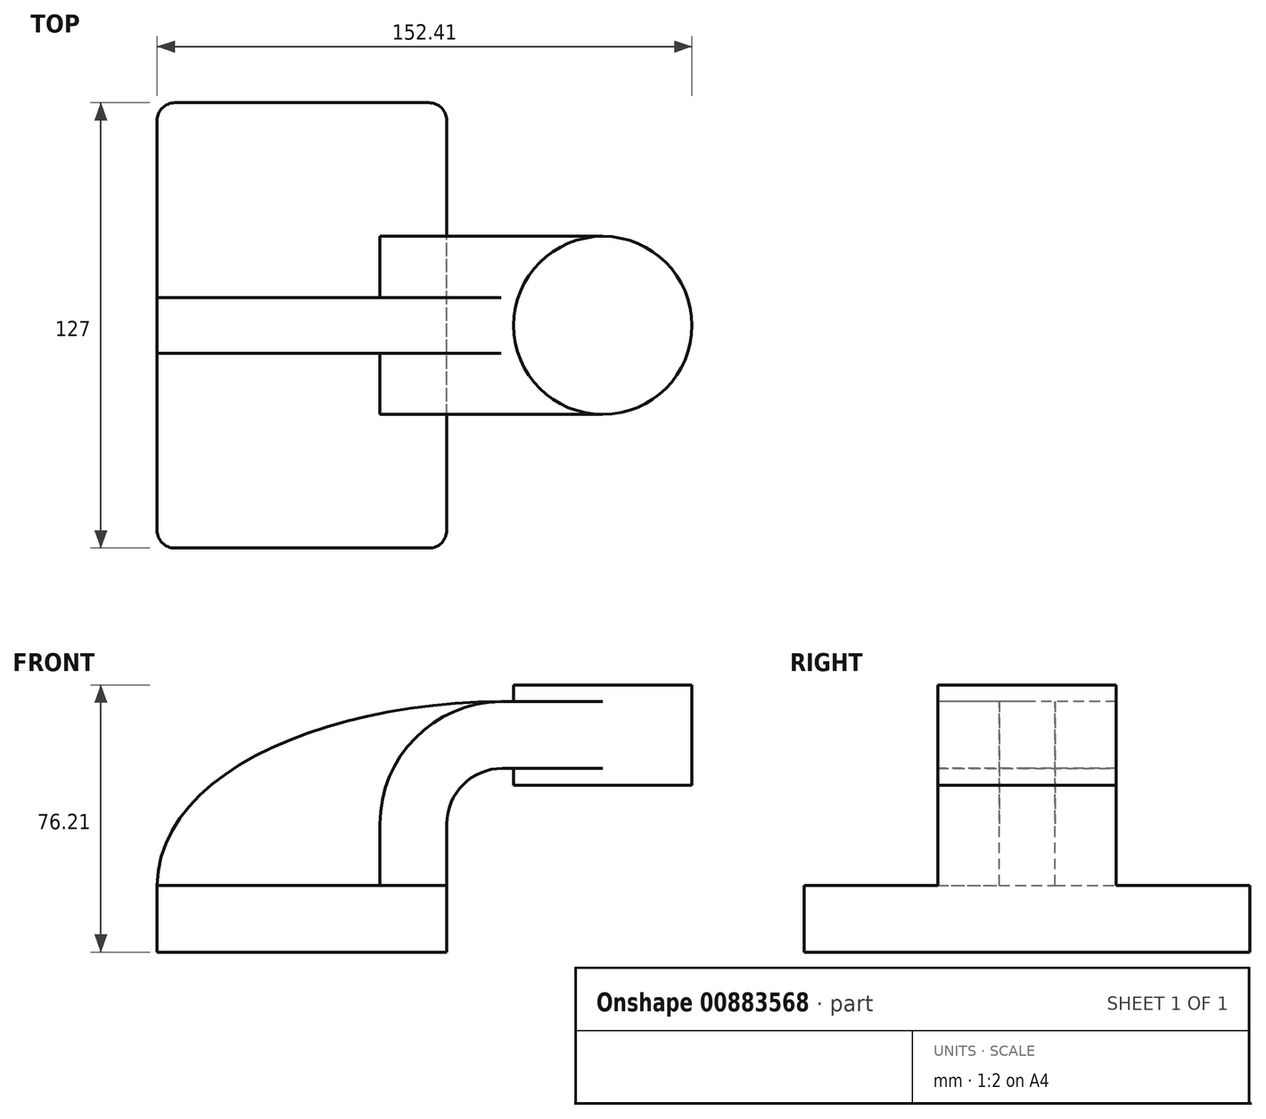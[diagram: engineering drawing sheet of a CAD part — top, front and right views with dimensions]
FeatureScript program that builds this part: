
annotation { "Feature Type Name" : "Feature", "Feature Type Description" : "" }
export const myFeature = defineFeature(function(context is Context, id is Id, definition is map)
    precondition{}
    {
        {
            var Q0;
            Q0=qCreatedBy(makeId("Front.planeOp"),FACE);
            var sketch = newSketch(context, id + "F0", { "sketchPlane" : qUnion([Q0])});
            skLineSegment(sketch, "E0.bottom", {"start": v(-41.28, -9.53) * mm, "end": v(41.28, -9.53) * mm});
            skLineSegment(sketch, "E0.top", {"start": v(-41.28, 9.52) * mm, "end": v(41.28, 9.52) * mm});
            skLineSegment(sketch, "E0.left", {"start": v(-41.28, -9.53) * mm, "end": v(-41.28, 9.53) * mm});
            skLineSegment(sketch, "E0.right", {"start": v(41.28, -9.53) * mm, "end": v(41.28, 9.52) * mm});
            skPoint(sketch, "E0.middle", {"position": v(0, 0) * mm});
            skLineSegment(sketch, "E1.bottom", {"start": v(111.12, 38.1) * mm, "end": v(60.32, 38.1) * mm});
            skLineSegment(sketch, "E1.top", {"start": v(111.12, 66.67) * mm, "end": v(60.32, 66.67) * mm});
            skLineSegment(sketch, "E1.left", {"start": v(111.12, 38.1) * mm, "end": v(111.12, 66.68) * mm});
            skLineSegment(sketch, "E1.right", {"start": v(60.32, 38.1) * mm, "end": v(60.32, 66.68) * mm});
            skPoint(sketch, "E1.middle", {"position": v(85.72, 52.39) * mm});
            skLineSegment(sketch, "E2", {"start": v(41.28, 9.52) * mm, "end": v(41.28, 27) * mm});
            skArc(sketch, "E3", {"start": v(41.27, 27) * mm, "mid": v(45.92, 38.23) * mm, "end": v(57.15, 42.88) * mm});
            skLineSegment(sketch, "E4", {"start": v(57.15, 42.88) * mm, "end": v(85.72, 42.88) * mm});
            skLineSegment(sketch, "E5.0", {"start": v(57.15, 61.93) * mm, "end": v(85.72, 61.93) * mm});
            skArc(sketch, "E5.1", {"start": v(22.22, 27) * mm, "mid": v(32.45, 51.7) * mm, "end": v(57.15, 61.93) * mm});
            skLineSegment(sketch, "E5.2", {"start": v(22.22, 9.52) * mm, "end": v(22.22, 27) * mm});
            skLineSegment(sketch, "E6", {"start": v(85.72, 38.1) * mm, "end": v(85.72, 66.67) * mm});
            skFitSpline(sketch, "E7", {"points": [v(-41.28, 9.52) * mm, v(57.15, 61.93) * mm], "startDerivative": vector(1.2, 96.26) * mm, "endDerivative": vector(151.74, 0.75) * mm});
            skSolve(sketch);
        }
        {
            var Q0;
            Q0=makeQuery(id+"F0.imprint","IMPRINT",FACE,{"disambiguationData":[TD([[makeQuery(id+"F0.imprint","IMPRINT",EDGE,{"derivedFrom":sQuery(id+"F0.wireOp",EDGE,"E0.bottom")}),1.0]])]});
            extrude(context, id + "F1", {"entities" : qUnion([Q0]), "endBound" : BoundingType.SYMMETRIC, "depth" : 127 * mm, "offsetDistance" : 25.4 * mm});
        }
        {
            var Q0;
            {var subQ1=sQuery(id+"F0.wireOp",EDGE,"E2");Q0=makeQuery(id+"F0.imprint","IMPRINT",FACE,{"disambiguationData":[TD([[makeQuery(id+"F0.imprint","IMPRINT",EDGE,{"derivedFrom":subQ1}),1.0]])]});}
            var Q1;
            {var subQ0=sQuery(id+"F0.wireOp",EDGE,"E4");var subQ1=sQuery(id+"F0.wireOp",EDGE,"E1.right");var subQ2=makeQuery(id+"F0.imprint","INTERSECT",VERTEX,{"derivedFrom":[subQ1,subQ0]});Q1=makeQuery(id+"F0.imprint","IMPRINT",FACE,{"disambiguationData":[TD([[makeQuery(id+"F0.imprint","IMPRINT",EDGE,{"disambiguationData":[TD([[subQ2,-1.0]])],"derivedFrom":subQ1}),-1.0]])]});}
            extrude(context, id + "F2", {"entities" : qUnion([Q0, Q1]), "operationType" : NewBodyOperationType.ADD, "endBound" : BoundingType.SYMMETRIC, "depth" : 50.8 * mm, "offsetDistance" : 25.4 * mm});
        }
        {
            var Q0;
            {var subQ3=sQuery(id+"F0.wireOp",EDGE,"E5.2");Q0=makeQuery(id+"F0.imprint","IMPRINT",FACE,{"disambiguationData":[TD([[makeQuery(id+"F0.imprint","IMPRINT",EDGE,{"derivedFrom":subQ3}),1.0]])]});}
            extrude(context, id + "F3", {"entities" : qUnion([Q0]), "operationType" : NewBodyOperationType.ADD, "endBound" : BoundingType.SYMMETRIC, "depth" : 15.88 * mm, "offsetDistance" : 25.4 * mm});
        }
        {
            var Q0;
            {var subQ0=sQuery(id+"F0.wireOp",EDGE,"E1.left");Q0=makeQuery(id+"F0.imprint","IMPRINT",FACE,{"disambiguationData":[TD([[makeQuery(id+"F0.imprint","IMPRINT",EDGE,{"derivedFrom":subQ0}),1.0]])]});}
            var Q1;
            Q1=sQuery(id+"F0.wireOp",EDGE,"E6");
            revolve(context, id + "F4", {"operationType" : NewBodyOperationType.ADD, "surfaceOperationType" : NewSurfaceOperationType.NEW, "entities" : qUnion([Q0]), "axis" : qUnion([Q1]), "revolveType" : RevolveType.FULL});
        }
        {
            var Q0;
            Q0=makeQuery(id+"F1.opExtrude","CAP_EDGE",EDGE,{"disambiguationData":[OSD([sQuery(id+"F0.wireOp",EDGE,"E0.right")])],"isStart":false});
            var Q1;
            Q1=makeQuery(id+"F1.opExtrude","CAP_EDGE",EDGE,{"disambiguationData":[OSD([sQuery(id+"F0.wireOp",EDGE,"E0.left")])],"isStart":false});
            var Q2;
            Q2=makeQuery(id+"F1.opExtrude","CAP_EDGE",EDGE,{"disambiguationData":[OSD([sQuery(id+"F0.wireOp",EDGE,"E0.right")])],"isStart":true});
            var Q3;
            Q3=makeQuery(id+"F1.opExtrude","CAP_EDGE",EDGE,{"disambiguationData":[OSD([sQuery(id+"F0.wireOp",EDGE,"E0.left")])],"isStart":true});
            fillet(context, id + "F5", {"entities" : qUnion([Q0, Q1, Q2, Q3]), "radius" : 5.08 * mm, "tangentPropagation" : true, "allowEdgeOverflow" : false});
        }
    });
